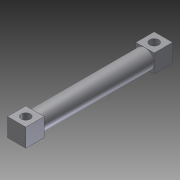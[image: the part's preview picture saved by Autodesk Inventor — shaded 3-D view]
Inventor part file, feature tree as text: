
AUTODESK INVENTOR PART (.ipt)
format: ipt  version: 2012 (Build 160160000, 160)  size: 101,376 bytes
history: native  units: in
note: dims shown in document units (in); Inventor stores cm internally (conversion verified against a paired STEP export)
features: extrude x4, sketch x4
ambient origin geometry x8: Origin, YZ Plane, XZ Plane, XY Plane, X Axis, Y Axis, Z Axis, Center Point
bodies: Solid1 (feature_tree)
feature tree (8):
  extrude  "Extrusion1"  Depth=3.0in TaperAngle=0.0deg
  extrude  "Extrusion2"  Depth=0.5in TaperAngle=0.0deg
  extrude  "Extrusion3"  Depth=0.25in
  extrude  "Extrusion4"  Depth=0.25in
  sketch  "Sketch1"  dims[d0=0.5in d1=3.0in d2=0.0in]
  sketch  "Sketch2"  dims[d3=0.5in d4=0.0in d5=0.5in d6=0.0in]
  sketch  "Sketch3"  dims[d7=0.25in d8=0.25in]
  sketch  "Sketch4"  dims[d9=0.25in d10=0.25in d11=0.25in d12=1.0in d13=0.0in]
